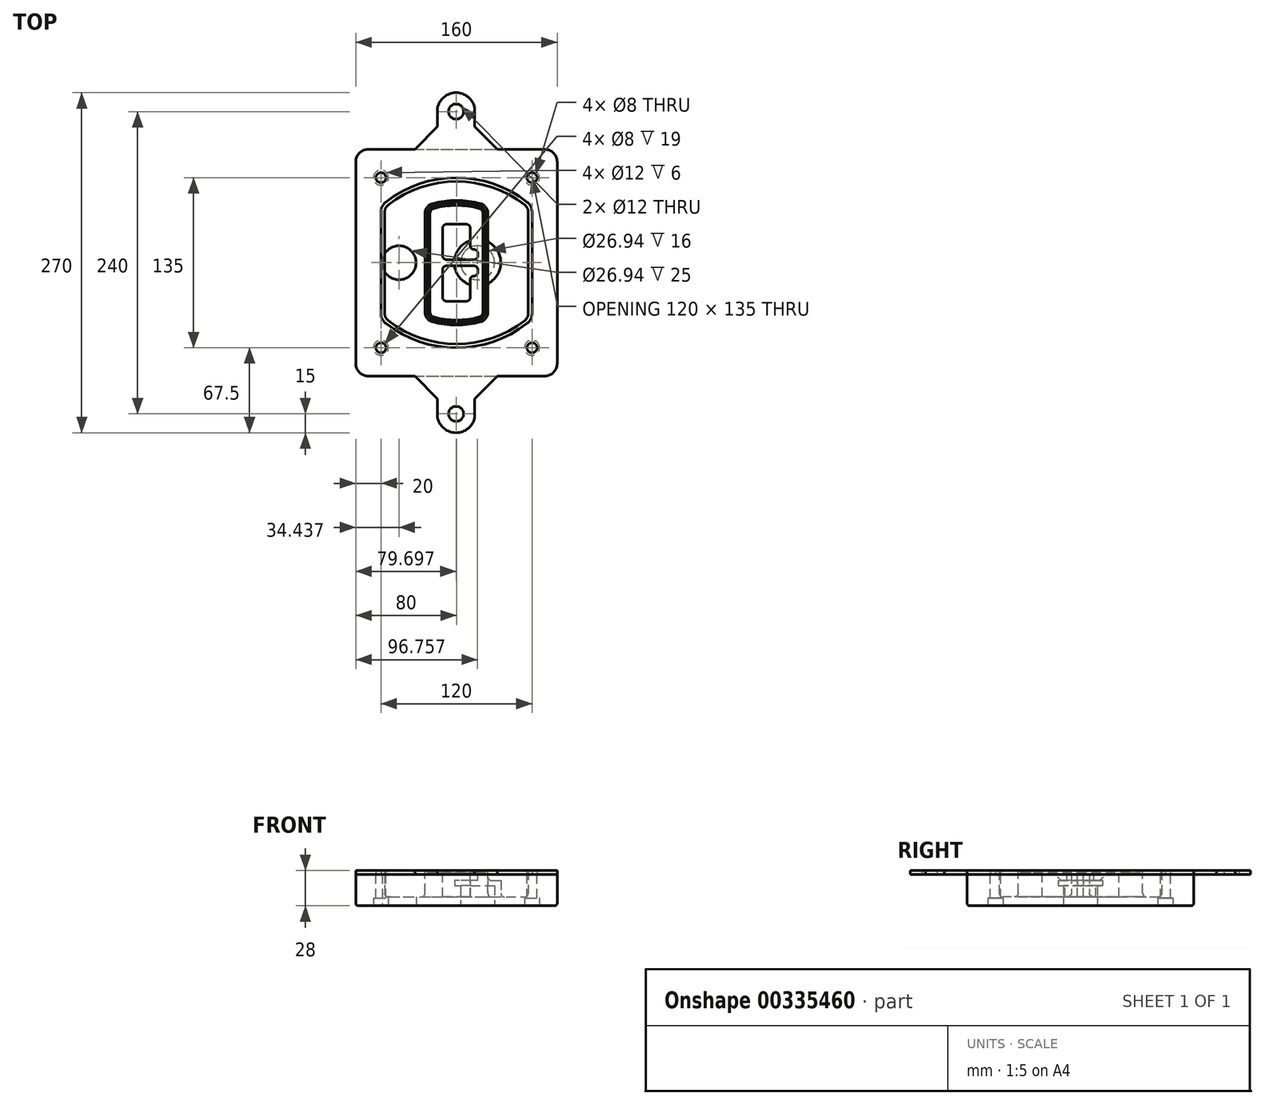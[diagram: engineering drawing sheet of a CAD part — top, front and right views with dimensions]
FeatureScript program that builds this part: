
annotation { "Feature Type Name" : "Feature", "Feature Type Description" : "" }
export const myFeature = defineFeature(function(context is Context, id is Id, definition is map)
    precondition{}
    {
        {
            var Q0;
            Q0=qCreatedBy(makeId("Top.planeOp"),FACE);
            var sketch = newSketch(context, id + "F0", { "sketchPlane" : qUnion([Q0])});
            skPoint(sketch, "E0.rect.middle", {"position": v(0, 0) * mm});
            skLineSegment(sketch, "E1.bottom", {"start": v(-70, -90) * mm, "end": v(70, -90) * mm});
            skLineSegment(sketch, "E1.top", {"start": v(-70, 90) * mm, "end": v(70, 90) * mm});
            skLineSegment(sketch, "E1.left", {"start": v(-80, -80) * mm, "end": v(-80, 80) * mm});
            skLineSegment(sketch, "E1.right", {"start": v(80, -80) * mm, "end": v(80, 80) * mm});
            skLineSegment(sketch, "E2", {"start": v(-80, 90) * mm, "end": v(80, -90) * mm, "construction": true});
            skLineSegment(sketch, "E3", {"start": v(80, 90) * mm, "end": v(-80, -90) * mm, "construction": true});
            skCircle(sketch, "E4", {"center": v(-60, 67.5) * mm, "radius": 4 * mm});
            skCircle(sketch, "E5", {"center": v(60, 67.5) * mm, "radius": 4 * mm});
            skCircle(sketch, "E6", {"center": v(60, -67.5) * mm, "radius": 4 * mm});
            skCircle(sketch, "E7", {"center": v(-60, -67.5) * mm, "radius": 4 * mm});
            skLineSegment(sketch, "E8", {"start": v(-60, 67.5) * mm, "end": v(60, 67.5) * mm, "construction": true});
            skLineSegment(sketch, "E9", {"start": v(60, 67.5) * mm, "end": v(60, -67.5) * mm, "construction": true});
            skLineSegment(sketch, "E10", {"start": v(60, -67.5) * mm, "end": v(-60, -67.5) * mm, "construction": true});
            skLineSegment(sketch, "E11", {"start": v(-60, -67.5) * mm, "end": v(-60, 67.5) * mm, "construction": true});
            skLineSegment(sketch, "E12", {"start": v(-60, 40.3) * mm, "end": v(-60, -40.3) * mm});
            skLineSegment(sketch, "E13", {"start": v(60, 40.3) * mm, "end": v(60, -40.3) * mm});
            skArc(sketch, "E14", {"start": v(56.15, 48.18) * mm, "mid": v(0, 67.5) * mm, "end": v(-56.15, 48.18) * mm});
            skArc(sketch, "E15", {"start": v(-56.15, -48.18) * mm, "mid": v(0, -67.5) * mm, "end": v(56.15, -48.18) * mm});
            skLineSegment(sketch, "E16", {"start": v(-60, 0) * mm, "end": v(60, 0) * mm, "construction": true});
            skPoint(sketch, "E17.visualSharp", {"position": v(-60, -45) * mm});
            skArc(sketch, "E17.filletArc", {"start": v(-60, -40.3) * mm, "mid": v(-58.99, -44.68) * mm, "end": v(-56.15, -48.18) * mm});
            skPoint(sketch, "E18.visualSharp", {"position": v(-60, 45) * mm});
            skArc(sketch, "E18.filletArc", {"start": v(-56.15, 48.18) * mm, "mid": v(-58.99, 44.68) * mm, "end": v(-60, 40.3) * mm});
            skPoint(sketch, "E19.visualSharp", {"position": v(60, 45) * mm});
            skArc(sketch, "E19.filletArc", {"start": v(60, 40.3) * mm, "mid": v(58.99, 44.68) * mm, "end": v(56.15, 48.18) * mm});
            skPoint(sketch, "E20.visualSharp", {"position": v(60, -45) * mm});
            skArc(sketch, "E20.filletArc", {"start": v(56.15, -48.18) * mm, "mid": v(58.99, -44.68) * mm, "end": v(60, -40.3) * mm});
            skPoint(sketch, "E21.visualSharp", {"position": v(-80, 90) * mm});
            skArc(sketch, "E21.filletArc", {"start": v(-70, 90) * mm, "mid": v(-77.07, 87.07) * mm, "end": v(-80, 80) * mm});
            skPoint(sketch, "E22.visualSharp", {"position": v(80, 90) * mm});
            skArc(sketch, "E22.filletArc", {"start": v(80, 80) * mm, "mid": v(77.07, 87.07) * mm, "end": v(70, 90) * mm});
            skPoint(sketch, "E23.visualSharp", {"position": v(80, -90) * mm});
            skArc(sketch, "E23.filletArc", {"start": v(70, -90) * mm, "mid": v(77.07, -87.07) * mm, "end": v(80, -80) * mm});
            skPoint(sketch, "E24.visualSharp", {"position": v(-80, -90) * mm});
            skArc(sketch, "E24.filletArc", {"start": v(-80, -80) * mm, "mid": v(-77.07, -87.07) * mm, "end": v(-70, -90) * mm});
            skArc(sketch, "E25.0", {"start": v(57, 40.3) * mm, "mid": v(56.3, 43.36) * mm, "end": v(54.3, 45.81) * mm});
            skLineSegment(sketch, "E25.1", {"start": v(57, 40.3) * mm, "end": v(57, -40.3) * mm});
            skArc(sketch, "E25.2", {"start": v(54.3, -45.81) * mm, "mid": v(56.3, -43.36) * mm, "end": v(57, -40.3) * mm});
            skArc(sketch, "E25.3", {"start": v(-54.3, -45.81) * mm, "mid": v(0, -64.5) * mm, "end": v(54.3, -45.81) * mm});
            skArc(sketch, "E25.4", {"start": v(-57, -40.3) * mm, "mid": v(-56.3, -43.36) * mm, "end": v(-54.3, -45.81) * mm});
            skArc(sketch, "E25.5", {"start": v(54.3, 45.81) * mm, "mid": v(0, 64.5) * mm, "end": v(-54.3, 45.81) * mm});
            skLineSegment(sketch, "E25.6", {"start": v(-57, 40.3) * mm, "end": v(-57, -40.3) * mm});
            skArc(sketch, "E25.7", {"start": v(-54.3, 45.81) * mm, "mid": v(-56.3, 43.36) * mm, "end": v(-57, 40.3) * mm});
            skArc(sketch, "E26.0", {"start": v(-58.62, 51.33) * mm, "mid": v(-62.58, 46.43) * mm, "end": v(-64, 40.3) * mm});
            skArc(sketch, "E26.1", {"start": v(58.62, 51.33) * mm, "mid": v(0, 71.5) * mm, "end": v(-58.62, 51.33) * mm});
            skArc(sketch, "E26.2", {"start": v(64, 40.3) * mm, "mid": v(62.58, 46.43) * mm, "end": v(58.62, 51.33) * mm});
            skLineSegment(sketch, "E26.3", {"start": v(64, 40.3) * mm, "end": v(64, -40.3) * mm});
            skArc(sketch, "E26.4", {"start": v(58.62, -51.33) * mm, "mid": v(62.58, -46.43) * mm, "end": v(64, -40.3) * mm});
            skLineSegment(sketch, "E26.5", {"start": v(-64, 40.3) * mm, "end": v(-64, -40.3) * mm});
            skArc(sketch, "E26.6", {"start": v(-58.62, -51.33) * mm, "mid": v(0, -71.5) * mm, "end": v(58.62, -51.33) * mm});
            skArc(sketch, "E26.7", {"start": v(-64, -40.3) * mm, "mid": v(-62.58, -46.43) * mm, "end": v(-58.62, -51.33) * mm});
            skSolve(sketch);
        }
        {
            var Q0;
            Q0=makeQuery(id+"F0.imprint","IMPRINT",FACE,{"disambiguationData":[TD([[makeQuery(id+"F0.imprint","IMPRINT",EDGE,{"derivedFrom":sQuery(id+"F0.wireOp",EDGE,"E1.bottom")}),1.0]])]});
            var Q1;
            Q1=makeQuery(id+"F0.imprint","IMPRINT",FACE,{"disambiguationData":[TD([[makeQuery(id+"F0.imprint","IMPRINT",EDGE,{"derivedFrom":sQuery(id+"F0.wireOp",EDGE,"E12")}),1.0]])]});
            var Q2;
            Q2=makeQuery(id+"F0.imprint","IMPRINT",FACE,{"disambiguationData":[TD([[makeQuery(id+"F0.imprint","IMPRINT",EDGE,{"derivedFrom":sQuery(id+"F0.wireOp",EDGE,"E25.0")}),1.0]])]});
            var Q3;
            Q3=makeQuery(id+"F0.imprint","IMPRINT",FACE,{"disambiguationData":[TD([[makeQuery(id+"F0.imprint","IMPRINT",EDGE,{"derivedFrom":sQuery(id+"F0.wireOp",EDGE,"E12")}),-1.0]])]});
            extrude(context, id + "F1", {"entities" : qUnion([Q0, Q1, Q2, Q3]), "oppositeDirection" : true, "depth" : 25 * mm});
        }
        {
            var Q0;
            Q0=makeQuery(id+"F0.imprint","IMPRINT",FACE,{"disambiguationData":[TD([[makeQuery(id+"F0.imprint","IMPRINT",EDGE,{"derivedFrom":sQuery(id+"F0.wireOp",EDGE,"E12")}),1.0]])]});
            extrude(context, id + "F2", {"entities" : qUnion([Q0]), "operationType" : NewBodyOperationType.ADD, "depth" : 3 * mm});
        }
        {
            var Q0;
            Q0=makeQuery(id+"F0.imprint","IMPRINT",FACE,{"disambiguationData":[TD([[makeQuery(id+"F0.imprint","IMPRINT",EDGE,{"derivedFrom":sQuery(id+"F0.wireOp",EDGE,"E25.0")}),1.0]])]});
            extrude(context, id + "F3", {"entities" : qUnion([Q0]), "operationType" : NewBodyOperationType.REMOVE, "oppositeDirection" : true, "depth" : 18 * mm});
        }
        {
            var Q0;
            Q0=makeQuery(id+"F2.opExtrude","CAP_FACE",FACE,{"disambiguationData":[OSD([sQuery(id+"F0.wireOp",EDGE,"E12"),sQuery(id+"F0.wireOp",EDGE,"E13"),sQuery(id+"F0.wireOp",EDGE,"E14"),sQuery(id+"F0.wireOp",EDGE,"E15"),sQuery(id+"F0.wireOp",EDGE,"E17.filletArc"),sQuery(id+"F0.wireOp",EDGE,"E18.filletArc"),sQuery(id+"F0.wireOp",EDGE,"E19.filletArc"),sQuery(id+"F0.wireOp",EDGE,"E20.filletArc"),sQuery(id+"F0.wireOp",EDGE,"E25.0"),sQuery(id+"F0.wireOp",EDGE,"E25.1"),sQuery(id+"F0.wireOp",EDGE,"E25.2"),sQuery(id+"F0.wireOp",EDGE,"E25.3"),sQuery(id+"F0.wireOp",EDGE,"E25.4"),sQuery(id+"F0.wireOp",EDGE,"E25.5"),sQuery(id+"F0.wireOp",EDGE,"E25.6"),sQuery(id+"F0.wireOp",EDGE,"E25.7")])],"isStart":false});
            var sketch = newSketch(context, id + "F4", { "sketchPlane" : qUnion([Q0])});
            skArc(sketch, "E27.0", {"start": v(-19.08, -46.97) * mm, "mid": v(0, -49.5) * mm, "end": v(19.08, -46.97) * mm});
            skArc(sketch, "E28.0", {"start": v(19.08, 46.97) * mm, "mid": v(0, 49.5) * mm, "end": v(-19.08, 46.97) * mm});
            skLineSegment(sketch, "E29", {"start": v(-25, 39.25) * mm, "end": v(-25, -39.25) * mm});
            skLineSegment(sketch, "E30", {"start": v(25, 39.25) * mm, "end": v(25, -39.25) * mm});
            skLineSegment(sketch, "E31", {"start": v(-25, 45.1) * mm, "end": v(25, 45.1) * mm, "construction": true});
            skLineSegment(sketch, "E32", {"start": v(-25, -45.1) * mm, "end": v(25, -45.1) * mm, "construction": true});
            skPoint(sketch, "E33.visualSharp", {"position": v(-25, 45.1) * mm});
            skArc(sketch, "E33.filletArc", {"start": v(-19.08, 46.97) * mm, "mid": v(-23.35, 44.11) * mm, "end": v(-25, 39.25) * mm});
            skPoint(sketch, "E34.visualSharp", {"position": v(25, 45.1) * mm});
            skArc(sketch, "E34.filletArc", {"start": v(25, 39.25) * mm, "mid": v(23.35, 44.11) * mm, "end": v(19.08, 46.97) * mm});
            skPoint(sketch, "E35.visualSharp", {"position": v(25, -45.1) * mm});
            skArc(sketch, "E35.filletArc", {"start": v(19.08, -46.97) * mm, "mid": v(23.35, -44.11) * mm, "end": v(25, -39.25) * mm});
            skPoint(sketch, "E36.visualSharp", {"position": v(-25, -45.1) * mm});
            skArc(sketch, "E36.filletArc", {"start": v(-25, -39.25) * mm, "mid": v(-23.35, -44.11) * mm, "end": v(-19.08, -46.97) * mm});
            skArc(sketch, "E37.0", {"start": v(54.3, 45.81) * mm, "mid": v(0, 64.5) * mm, "end": v(-54.3, 45.81) * mm});
            skArc(sketch, "E37.1", {"start": v(-54.3, 45.81) * mm, "mid": v(-56.3, 43.36) * mm, "end": v(-57, 40.3) * mm});
            skLineSegment(sketch, "E37.2", {"start": v(-57, 40.3) * mm, "end": v(-57, -40.3) * mm});
            skArc(sketch, "E37.3", {"start": v(-57, -40.3) * mm, "mid": v(-56.3, -43.36) * mm, "end": v(-54.3, -45.81) * mm});
            skArc(sketch, "E37.4", {"start": v(-54.3, -45.81) * mm, "mid": v(0, -64.5) * mm, "end": v(54.3, -45.81) * mm});
            skArc(sketch, "E37.5", {"start": v(54.3, -45.81) * mm, "mid": v(56.3, -43.36) * mm, "end": v(57, -40.3) * mm});
            skLineSegment(sketch, "E37.6", {"start": v(57, 40.3) * mm, "end": v(57, -40.3) * mm});
            skArc(sketch, "E37.7", {"start": v(57, 40.3) * mm, "mid": v(56.3, 43.36) * mm, "end": v(54.3, 45.81) * mm});
            skLineSegment(sketch, "E38.0", {"start": v(23, 39.25) * mm, "end": v(23, -39.25) * mm});
            skArc(sketch, "E38.1", {"start": v(18.56, -45.04) * mm, "mid": v(21.76, -42.9) * mm, "end": v(23, -39.25) * mm});
            skArc(sketch, "E38.2", {"start": v(-18.56, -45.04) * mm, "mid": v(0, -47.5) * mm, "end": v(18.56, -45.04) * mm});
            skArc(sketch, "E38.3", {"start": v(-23, -39.25) * mm, "mid": v(-21.76, -42.9) * mm, "end": v(-18.56, -45.04) * mm});
            skLineSegment(sketch, "E38.4", {"start": v(-23, 39.25) * mm, "end": v(-23, -39.25) * mm});
            skArc(sketch, "E38.5", {"start": v(23, 39.25) * mm, "mid": v(21.76, 42.9) * mm, "end": v(18.56, 45.04) * mm});
            skArc(sketch, "E38.6", {"start": v(-18.56, 45.04) * mm, "mid": v(-21.76, 42.9) * mm, "end": v(-23, 39.25) * mm});
            skArc(sketch, "E38.7", {"start": v(18.56, 45.04) * mm, "mid": v(0, 47.5) * mm, "end": v(-18.56, 45.04) * mm});
            skArc(sketch, "E39.0", {"start": v(21, 39.25) * mm, "mid": v(20.18, 41.68) * mm, "end": v(18.04, 43.1) * mm});
            skLineSegment(sketch, "E39.1", {"start": v(21, 39.25) * mm, "end": v(21, -39.25) * mm});
            skArc(sketch, "E39.2", {"start": v(18.04, -43.1) * mm, "mid": v(20.18, -41.68) * mm, "end": v(21, -39.25) * mm});
            skArc(sketch, "E39.3", {"start": v(-18.04, -43.1) * mm, "mid": v(0, -45.5) * mm, "end": v(18.04, -43.1) * mm});
            skArc(sketch, "E39.4", {"start": v(-21, -39.25) * mm, "mid": v(-20.18, -41.68) * mm, "end": v(-18.04, -43.1) * mm});
            skArc(sketch, "E39.5", {"start": v(18.04, 43.1) * mm, "mid": v(0, 45.5) * mm, "end": v(-18.04, 43.1) * mm});
            skLineSegment(sketch, "E39.6", {"start": v(-21, 39.25) * mm, "end": v(-21, -39.25) * mm});
            skArc(sketch, "E39.7", {"start": v(-18.04, 43.1) * mm, "mid": v(-20.18, 41.68) * mm, "end": v(-21, 39.25) * mm});
            skLineSegment(sketch, "E40", {"start": v(-25, 0) * mm, "end": v(25, 0) * mm, "construction": true});
            skLineSegment(sketch, "E41", {"start": v(-11, 5.5) * mm, "end": v(-11, 27.5) * mm});
            skLineSegment(sketch, "E42", {"start": v(-8, 30.5) * mm, "end": v(8, 30.5) * mm});
            skLineSegment(sketch, "E43", {"start": v(11, 27.5) * mm, "end": v(11, 13.5) * mm});
            skLineSegment(sketch, "E44", {"start": v(14, 10.5) * mm, "end": v(14, 10.5) * mm});
            skLineSegment(sketch, "E45", {"start": v(17, 7.5) * mm, "end": v(17, 5.5) * mm});
            skLineSegment(sketch, "E46", {"start": v(14, 2.5) * mm, "end": v(-8, 2.5) * mm});
            skPoint(sketch, "E47.visualSharp", {"position": v(-11, 30.5) * mm});
            skArc(sketch, "E47.filletArc", {"start": v(-8, 30.5) * mm, "mid": v(-10.12, 29.62) * mm, "end": v(-11, 27.5) * mm});
            skPoint(sketch, "E48.visualSharp", {"position": v(11, 30.5) * mm});
            skArc(sketch, "E48.filletArc", {"start": v(11, 27.5) * mm, "mid": v(10.12, 29.62) * mm, "end": v(8, 30.5) * mm});
            skPoint(sketch, "E49.visualSharp", {"position": v(11, 10.5) * mm});
            skArc(sketch, "E49.filletArc", {"start": v(11, 13.5) * mm, "mid": v(11.88, 11.38) * mm, "end": v(14, 10.5) * mm});
            skPoint(sketch, "E50.visualSharp", {"position": v(17, 10.5) * mm});
            skArc(sketch, "E50.filletArc", {"start": v(17, 7.5) * mm, "mid": v(16.12, 9.62) * mm, "end": v(14, 10.5) * mm});
            skPoint(sketch, "E51.visualSharp", {"position": v(17, 2.5) * mm});
            skArc(sketch, "E51.filletArc", {"start": v(14, 2.5) * mm, "mid": v(16.12, 3.38) * mm, "end": v(17, 5.5) * mm});
            skPoint(sketch, "E52.visualSharp", {"position": v(-11, 2.5) * mm});
            skArc(sketch, "E52.filletArc", {"start": v(-11, 5.5) * mm, "mid": v(-10.12, 3.38) * mm, "end": v(-8, 2.5) * mm});
            skLineSegment(sketch, "E53.0.MirrorCS", {"start": v(14, -2.5) * mm, "end": v(-8, -2.5) * mm});
            skArc(sketch, "E54.0.MirrorCS", {"start": v(-11, -5.5) * mm, "mid": v(-10.12, -3.38) * mm, "end": v(-8, -2.5) * mm});
            skLineSegment(sketch, "E55.0.MirrorCS", {"start": v(-11, -5.5) * mm, "end": v(-11, -27.5) * mm});
            skArc(sketch, "E56.0.MirrorCS", {"start": v(-8, -30.5) * mm, "mid": v(-10.12, -29.62) * mm, "end": v(-11, -27.5) * mm});
            skLineSegment(sketch, "E57.0.MirrorCS", {"start": v(-8, -30.5) * mm, "end": v(8, -30.5) * mm});
            skArc(sketch, "E58.0.MirrorCS", {"start": v(11, -27.5) * mm, "mid": v(10.12, -29.62) * mm, "end": v(8, -30.5) * mm});
            skLineSegment(sketch, "E59.0.MirrorCS", {"start": v(11, -27.5) * mm, "end": v(11, -13.5) * mm});
            skArc(sketch, "E60.0.MirrorCS", {"start": v(11, -13.5) * mm, "mid": v(11.88, -11.38) * mm, "end": v(14, -10.5) * mm});
            skArc(sketch, "E61.0.MirrorCS", {"start": v(17, -7.5) * mm, "mid": v(16.12, -9.62) * mm, "end": v(14, -10.5) * mm});
            skLineSegment(sketch, "E62.0.MirrorCS", {"start": v(17, -7.5) * mm, "end": v(17, -5.5) * mm});
            skArc(sketch, "E63.0.MirrorCS", {"start": v(14, -2.5) * mm, "mid": v(16.12, -3.38) * mm, "end": v(17, -5.5) * mm});
            skSolve(sketch);
        }
        {
            var Q0;
            Q0=makeQuery(id+"F4.imprint","IMPRINT",FACE,{"disambiguationData":[TD([[makeQuery(id+"F4.imprint","IMPRINT",EDGE,{"derivedFrom":sQuery(id+"F4.wireOp",EDGE,"E27.0")}),1.0]])]});
            var Q1;
            Q1=makeQuery(id+"F4.imprint","IMPRINT",FACE,{"disambiguationData":[TD([[makeQuery(id+"F4.imprint","IMPRINT",EDGE,{"derivedFrom":sQuery(id+"F4.wireOp",EDGE,"E38.0")}),-1.0]])]});
            var Q2;
            Q2=makeQuery(id+"F4.imprint","IMPRINT",FACE,{"disambiguationData":[TD([[makeQuery(id+"F4.imprint","IMPRINT",EDGE,{"derivedFrom":sQuery(id+"F4.wireOp",EDGE,"E39.0")}),1.0]])]});
            extrude(context, id + "F5", {"entities" : qUnion([Q0, Q1, Q2]), "operationType" : NewBodyOperationType.ADD, "endBound" : BoundingType.UP_TO_NEXT, "oppositeDirection" : true, "depth" : 25 * mm});
        }
        {
            var Q0;
            Q0=makeQuery(id+"F4.imprint","IMPRINT",FACE,{"disambiguationData":[TD([[makeQuery(id+"F4.imprint","IMPRINT",EDGE,{"derivedFrom":sQuery(id+"F4.wireOp",EDGE,"E38.0")}),-1.0]])]});
            extrude(context, id + "F6", {"entities" : qUnion([Q0]), "operationType" : NewBodyOperationType.REMOVE, "oppositeDirection" : true, "depth" : 2 * mm});
        }
        {
            var Q0;
            Q0=makeQuery(id+"F1.opExtrude","CAP_FACE",FACE,{"disambiguationData":[OSD([sQuery(id+"F0.wireOp",EDGE,"E1.bottom"),sQuery(id+"F0.wireOp",EDGE,"E1.top"),sQuery(id+"F0.wireOp",EDGE,"E1.left"),sQuery(id+"F0.wireOp",EDGE,"E1.right"),sQuery(id+"F0.wireOp",EDGE,"E4"),sQuery(id+"F0.wireOp",EDGE,"E5"),sQuery(id+"F0.wireOp",EDGE,"E6"),sQuery(id+"F0.wireOp",EDGE,"E7"),sQuery(id+"F0.wireOp",EDGE,"E21.filletArc"),sQuery(id+"F0.wireOp",EDGE,"E22.filletArc"),sQuery(id+"F0.wireOp",EDGE,"E23.filletArc"),sQuery(id+"F0.wireOp",EDGE,"E24.filletArc")])],"isStart":false});
            var sketch = newSketch(context, id + "F7", { "sketchPlane" : qUnion([Q0])});
            skCircle(sketch, "E64", {"center": v(16.76, 0) * mm, "radius": 13.47 * mm});
            skCircle(sketch, "E65", {"center": v(-45.56, 0) * mm, "radius": 13.47 * mm});
            skLineSegment(sketch, "E66", {"start": v(80, 0) * mm, "end": v(-80, 0) * mm});
            skCircle(sketch, "E67", {"center": v(16.76, 0) * mm, "radius": 18.47 * mm});
            skCircle(sketch, "E68", {"center": v(60, -67.5) * mm, "radius": 6 * mm});
            skCircle(sketch, "E69", {"center": v(-60, -67.5) * mm, "radius": 6 * mm});
            skCircle(sketch, "E70", {"center": v(-60, 67.5) * mm, "radius": 6 * mm});
            skCircle(sketch, "E71", {"center": v(60, 67.5) * mm, "radius": 6 * mm});
            skSolve(sketch);
        }
        {
            var Q0;
            {var subQ1=sQuery(id+"F7.wireOp",EDGE,"E66");var subQ4=sQuery(id+"F7.wireOp",EDGE,"E64");var subQ6=makeQuery(id+"F7.imprint","INTERSECT",VERTEX,{"disambiguationData":[OD(0.0)],"derivedFrom":[subQ4,subQ1]});Q0=makeQuery(id+"F7.imprint","IMPRINT",FACE,{"disambiguationData":[TD([[makeQuery(id+"F7.imprint","IMPRINT",EDGE,{"disambiguationData":[TD([[subQ6,-1.0]])],"derivedFrom":subQ4}),-1.0]])]});}
            var Q1;
            {var subQ0=sQuery(id+"F7.wireOp",EDGE,"E66");var subQ1=sQuery(id+"F7.wireOp",EDGE,"E64");var subQ3=makeQuery(id+"F7.imprint","INTERSECT",VERTEX,{"disambiguationData":[OD(0.0)],"derivedFrom":[subQ1,subQ0]});Q1=makeQuery(id+"F7.imprint","IMPRINT",FACE,{"disambiguationData":[TD([[makeQuery(id+"F7.imprint","IMPRINT",EDGE,{"disambiguationData":[TD([[subQ3,-1.0]])],"derivedFrom":subQ1}),1.0]])]});}
            var Q2;
            {var subQ0=sQuery(id+"F7.wireOp",EDGE,"E66");var subQ1=sQuery(id+"F7.wireOp",EDGE,"E64");var subQ3=makeQuery(id+"F7.imprint","INTERSECT",VERTEX,{"disambiguationData":[OD(0.0)],"derivedFrom":[subQ1,subQ0]});Q2=makeQuery(id+"F7.imprint","IMPRINT",FACE,{"disambiguationData":[TD([[makeQuery(id+"F7.imprint","IMPRINT",EDGE,{"disambiguationData":[TD([[subQ3,1.0]])],"derivedFrom":subQ1}),1.0]])]});}
            var Q3;
            {var subQ1=sQuery(id+"F7.wireOp",EDGE,"E66");var subQ4=sQuery(id+"F7.wireOp",EDGE,"E64");var subQ6=makeQuery(id+"F7.imprint","INTERSECT",VERTEX,{"disambiguationData":[OD(0.0)],"derivedFrom":[subQ4,subQ1]});Q3=makeQuery(id+"F7.imprint","IMPRINT",FACE,{"disambiguationData":[TD([[makeQuery(id+"F7.imprint","IMPRINT",EDGE,{"disambiguationData":[TD([[subQ6,1.0]])],"derivedFrom":subQ4}),-1.0]])]});}
            extrude(context, id + "F8", {"entities" : qUnion([Q0, Q1, Q2, Q3]), "operationType" : NewBodyOperationType.ADD, "oppositeDirection" : true, "depth" : 20 * mm});
        }
        {
            var Q0;
            {var subQ0=sQuery(id+"F7.wireOp",EDGE,"E66");var subQ1=sQuery(id+"F7.wireOp",EDGE,"E64");var subQ3=makeQuery(id+"F7.imprint","INTERSECT",VERTEX,{"disambiguationData":[OD(0.0)],"derivedFrom":[subQ1,subQ0]});Q0=makeQuery(id+"F7.imprint","IMPRINT",FACE,{"disambiguationData":[TD([[makeQuery(id+"F7.imprint","IMPRINT",EDGE,{"disambiguationData":[TD([[subQ3,-1.0]])],"derivedFrom":subQ1}),1.0]])]});}
            var Q1;
            {var subQ0=sQuery(id+"F7.wireOp",EDGE,"E66");var subQ1=sQuery(id+"F7.wireOp",EDGE,"E64");var subQ3=makeQuery(id+"F7.imprint","INTERSECT",VERTEX,{"disambiguationData":[OD(0.0)],"derivedFrom":[subQ1,subQ0]});Q1=makeQuery(id+"F7.imprint","IMPRINT",FACE,{"disambiguationData":[TD([[makeQuery(id+"F7.imprint","IMPRINT",EDGE,{"disambiguationData":[TD([[subQ3,1.0]])],"derivedFrom":subQ1}),1.0]])]});}
            extrude(context, id + "F9", {"entities" : qUnion([Q0, Q1]), "operationType" : NewBodyOperationType.REMOVE, "oppositeDirection" : true, "depth" : 16 * mm});
        }
        {
            var Q0;
            {var subQ0=sQuery(id+"F7.wireOp",EDGE,"E66");var subQ1=sQuery(id+"F7.wireOp",EDGE,"E65");var subQ3=makeQuery(id+"F7.imprint","INTERSECT",VERTEX,{"disambiguationData":[OD(0.0)],"derivedFrom":[subQ1,subQ0]});Q0=makeQuery(id+"F7.imprint","IMPRINT",FACE,{"disambiguationData":[TD([[makeQuery(id+"F7.imprint","IMPRINT",EDGE,{"disambiguationData":[TD([[subQ3,-1.0]])],"derivedFrom":subQ1}),1.0]])]});}
            var Q1;
            {var subQ0=sQuery(id+"F7.wireOp",EDGE,"E66");var subQ1=sQuery(id+"F7.wireOp",EDGE,"E65");var subQ3=makeQuery(id+"F7.imprint","INTERSECT",VERTEX,{"disambiguationData":[OD(0.0)],"derivedFrom":[subQ1,subQ0]});Q1=makeQuery(id+"F7.imprint","IMPRINT",FACE,{"disambiguationData":[TD([[makeQuery(id+"F7.imprint","IMPRINT",EDGE,{"disambiguationData":[TD([[subQ3,1.0]])],"derivedFrom":subQ1}),1.0]])]});}
            extrude(context, id + "F10", {"entities" : qUnion([Q0, Q1]), "operationType" : NewBodyOperationType.REMOVE, "oppositeDirection" : true, "depth" : 25 * mm});
        }
        {
            var Q0;
            Q0=makeQuery(id+"F7.imprint","IMPRINT",FACE,{"disambiguationData":[TD([[makeQuery(id+"F7.imprint","IMPRINT",EDGE,{"derivedFrom":sQuery(id+"F7.wireOp",EDGE,"E68")}),1.0]])]});
            var Q1;
            Q1=makeQuery(id+"F7.imprint","IMPRINT",FACE,{"disambiguationData":[TD([[makeQuery(id+"F7.imprint","IMPRINT",EDGE,{"derivedFrom":makeQuery(id+"F1.opExtrude","CAP_EDGE",EDGE,{"disambiguationData":[OSD([sQuery(id+"F0.wireOp",EDGE,"E5")])],"isStart":false})}),-1.0]])]});
            var Q2;
            Q2=makeQuery(id+"F7.imprint","IMPRINT",FACE,{"disambiguationData":[TD([[makeQuery(id+"F7.imprint","IMPRINT",EDGE,{"derivedFrom":sQuery(id+"F7.wireOp",EDGE,"E69")}),1.0]])]});
            var Q3;
            Q3=makeQuery(id+"F7.imprint","IMPRINT",FACE,{"disambiguationData":[TD([[makeQuery(id+"F7.imprint","IMPRINT",EDGE,{"derivedFrom":makeQuery(id+"F1.opExtrude","CAP_EDGE",EDGE,{"disambiguationData":[OSD([sQuery(id+"F0.wireOp",EDGE,"E4")])],"isStart":false})}),-1.0]])]});
            var Q4;
            Q4=makeQuery(id+"F7.imprint","IMPRINT",FACE,{"disambiguationData":[TD([[makeQuery(id+"F7.imprint","IMPRINT",EDGE,{"derivedFrom":sQuery(id+"F7.wireOp",EDGE,"E70")}),1.0]])]});
            var Q5;
            Q5=makeQuery(id+"F7.imprint","IMPRINT",FACE,{"disambiguationData":[TD([[makeQuery(id+"F7.imprint","IMPRINT",EDGE,{"derivedFrom":makeQuery(id+"F1.opExtrude","CAP_EDGE",EDGE,{"disambiguationData":[OSD([sQuery(id+"F0.wireOp",EDGE,"E7")])],"isStart":false})}),-1.0]])]});
            var Q6;
            Q6=makeQuery(id+"F7.imprint","IMPRINT",FACE,{"disambiguationData":[TD([[makeQuery(id+"F7.imprint","IMPRINT",EDGE,{"derivedFrom":sQuery(id+"F7.wireOp",EDGE,"E71")}),1.0]])]});
            var Q7;
            Q7=makeQuery(id+"F7.imprint","IMPRINT",FACE,{"disambiguationData":[TD([[makeQuery(id+"F7.imprint","IMPRINT",EDGE,{"derivedFrom":makeQuery(id+"F1.opExtrude","CAP_EDGE",EDGE,{"disambiguationData":[OSD([sQuery(id+"F0.wireOp",EDGE,"E6")])],"isStart":false})}),-1.0]])]});
            extrude(context, id + "F11", {"entities" : qUnion([Q0, Q1, Q2, Q3, Q4, Q5, Q6, Q7]), "operationType" : NewBodyOperationType.REMOVE, "oppositeDirection" : true, "depth" : 6 * mm});
        }
        {
            var Q0;
            Q0=makeQuery(id+"F9.boolean.opBoolean","COPY",FACE,{"derivedFrom":makeQuery(id+"F9.opExtrude","CAP_FACE",FACE,{"disambiguationData":[OSD([sQuery(id+"F7.wireOp",EDGE,"E64")])],"isStart":false})});
            var sketch = newSketch(context, id + "F12", { "sketchPlane" : qUnion([Q0])});
            skArc(sketch, "E72.0", {"start": v(11, 17.55) * mm, "mid": v(2.57, 11.82) * mm, "end": v(-1.54, 2.5) * mm});
            skArc(sketch, "E72.1", {"start": v(-1.54, -2.5) * mm, "mid": v(2.57, -11.82) * mm, "end": v(11, -17.55) * mm});
            skLineSegment(sketch, "E73", {"start": v(-1.54, -2.5) * mm, "end": v(14, -2.5) * mm});
            skLineSegment(sketch, "E74.0", {"start": v(14, 2.5) * mm, "end": v(-1.54, 2.5) * mm});
            skArc(sketch, "E74.1", {"start": v(14, 2.5) * mm, "mid": v(16.12, 3.38) * mm, "end": v(17, 5.5) * mm});
            skLineSegment(sketch, "E74.2", {"start": v(17, 7.5) * mm, "end": v(17, 5.5) * mm});
            skArc(sketch, "E74.3", {"start": v(17, 7.5) * mm, "mid": v(16.12, 9.62) * mm, "end": v(14, 10.5) * mm});
            skArc(sketch, "E74.4", {"start": v(11, 13.5) * mm, "mid": v(11.88, 11.38) * mm, "end": v(14, 10.5) * mm});
            skLineSegment(sketch, "E74.5", {"start": v(11, 17.55) * mm, "end": v(11, 13.5) * mm});
            skLineSegment(sketch, "E74.7", {"start": v(14, -2.5) * mm, "end": v(-1.54, -2.5) * mm});
            skArc(sketch, "E74.8", {"start": v(14, -2.5) * mm, "mid": v(16.12, -3.38) * mm, "end": v(17, -5.5) * mm});
            skLineSegment(sketch, "E74.9", {"start": v(17, -7.5) * mm, "end": v(17, -5.5) * mm});
            skArc(sketch, "E74.10", {"start": v(17, -7.5) * mm, "mid": v(16.12, -9.62) * mm, "end": v(14, -10.5) * mm});
            skArc(sketch, "E74.11", {"start": v(11, -13.5) * mm, "mid": v(11.88, -11.38) * mm, "end": v(14, -10.5) * mm});
            skLineSegment(sketch, "E74.12", {"start": v(11, -17.55) * mm, "end": v(11, -13.5) * mm});
            skPoint(sketch, "E75.orphan", {"position": v(11, -27.5) * mm});
            skPoint(sketch, "E76.orphan", {"position": v(-8, -2.5) * mm});
            skPoint(sketch, "E77.orphan", {"position": v(-8, 2.5) * mm});
            skPoint(sketch, "E78.orphan", {"position": v(11, 27.5) * mm});
            skSolve(sketch);
        }
        {
            var Q0;
            {var subQ7=sQuery(id+"F12.wireOp",EDGE,"E72.0");var subQ14=sQuery(id+"F12.wireOp",EDGE,"E72.1");var subQ16=sQuery(id+"F12.wireOp",EDGE,"E74.1");var subQ18=sQuery(id+"F12.wireOp",EDGE,"E74.8");Q0=qUnion([makeQuery(id+"F12.imprint","IMPRINT",FACE,{"disambiguationData":[TD([[makeQuery(id+"F12.imprint","IMPRINT",EDGE,{"derivedFrom":subQ7}),1.0]])]}),makeQuery(id+"F12.imprint","IMPRINT",FACE,{"disambiguationData":[TD([[makeQuery(id+"F12.imprint","IMPRINT",EDGE,{"derivedFrom":subQ14}),1.0]])]}),makeQuery(id+"F12.imprint","IMPRINT",FACE,{"disambiguationData":[TD([[makeQuery(id+"F12.imprint","IMPRINT",EDGE,{"derivedFrom":subQ16}),1.0]])]}),makeQuery(id+"F12.imprint","IMPRINT",FACE,{"disambiguationData":[TD([[makeQuery(id+"F12.imprint","IMPRINT",EDGE,{"derivedFrom":subQ18}),-1.0]])]})]);}
            var Q1;
            Q1=makeQuery(id+"F5.boolean.opBoolean","SPLIT",FACE,{"disambiguationData":[TD([makeQuery(id+"F5.opExtrude","SWEPT_FACE",FACE,{"disambiguationData":[OSD([sQuery(id+"F4.wireOp",EDGE,"E41")])]})])],"derivedFrom":makeQuery(id+"F3.boolean.opBoolean","COPY",FACE,{"derivedFrom":makeQuery(id+"F3.opExtrude","CAP_FACE",FACE,{"disambiguationData":[OSD([sQuery(id+"F0.wireOp",EDGE,"E25.0"),sQuery(id+"F0.wireOp",EDGE,"E25.1"),sQuery(id+"F0.wireOp",EDGE,"E25.2"),sQuery(id+"F0.wireOp",EDGE,"E25.3"),sQuery(id+"F0.wireOp",EDGE,"E25.4"),sQuery(id+"F0.wireOp",EDGE,"E25.5"),sQuery(id+"F0.wireOp",EDGE,"E25.6"),sQuery(id+"F0.wireOp",EDGE,"E25.7")])],"isStart":false})})});
            extrude(context, id + "F13", {"entities" : qUnion([Q0]), "operationType" : NewBodyOperationType.REMOVE, "endBound" : BoundingType.UP_TO_SURFACE, "endBoundEntityFace" : qUnion([Q1]), "depth" : 25 * mm});
        }
        {
            var Q0;
            Q0=makeQuery(id+"F3.boolean.opBoolean","COPY",EDGE,{"derivedFrom":makeQuery(id+"F3.opExtrude","CAP_EDGE",EDGE,{"disambiguationData":[OSD([sQuery(id+"F0.wireOp",EDGE,"E25.6")])],"isStart":false})});
            var Q1;
            Q1=makeQuery(id+"F8.boolean.opBoolean","INTERSECT",EDGE,{"derivedFrom":[makeQuery(id+"F5.opExtrude","SWEPT_FACE",FACE,{"disambiguationData":[OSD([sQuery(id+"F4.wireOp",EDGE,"E30")])]}),makeQuery(id+"F8.opExtrude","CAP_FACE",FACE,{"disambiguationData":[OSD([sQuery(id+"F7.wireOp",EDGE,"E67")])],"isStart":false})]});
            var Q2;
            Q2=makeQuery(id+"F8.boolean.opBoolean","INTERSECT",EDGE,{"disambiguationData":[OD(1.0)],"derivedFrom":[makeQuery(id+"F5.opExtrude","SWEPT_FACE",FACE,{"disambiguationData":[OSD([sQuery(id+"F4.wireOp",EDGE,"E30")])]}),makeQuery(id+"F8.opExtrude","SWEPT_FACE",FACE,{"disambiguationData":[OSD([sQuery(id+"F7.wireOp",EDGE,"E67")])]})]});
            var Q3;
            {var subQ0=sQuery(id+"F4.wireOp",EDGE,"E30");Q3=makeQuery(id+"F8.boolean.opBoolean","SPLIT",EDGE,{"disambiguationData":[TD([makeQuery(id+"F5.opExtrude","SWEPT_FACE",FACE,{"disambiguationData":[OSD([sQuery(id+"F4.wireOp",EDGE,"E35.filletArc")])]})])],"derivedFrom":makeQuery(id+"F5.opExtrude","CAP_EDGE",EDGE,{"disambiguationData":[OSD([subQ0])],"isStart":false})});}
            var Q4;
            {var subQ0=sQuery(id+"F0.wireOp",EDGE,"E25.7");var subQ1=sQuery(id+"F0.wireOp",EDGE,"E25.1");var subQ2=sQuery(id+"F0.wireOp",EDGE,"E25.6");var subQ3=sQuery(id+"F0.wireOp",EDGE,"E25.5");var subQ4=sQuery(id+"F0.wireOp",EDGE,"E25.4");var subQ5=sQuery(id+"F0.wireOp",EDGE,"E25.0");var subQ6=sQuery(id+"F0.wireOp",EDGE,"E25.2");var subQ7=sQuery(id+"F0.wireOp",EDGE,"E25.3");Q4=makeQuery(id+"F8.boolean.opBoolean","INTERSECT",EDGE,{"derivedFrom":[makeQuery(id+"F5.boolean.opBoolean","SPLIT",FACE,{"disambiguationData":[TD([makeQuery(id+"F2.opExtrude","SWEPT_FACE",FACE,{"disambiguationData":[OSD([subQ5])]})])],"derivedFrom":makeQuery(id+"F3.boolean.opBoolean","COPY",FACE,{"derivedFrom":makeQuery(id+"F3.opExtrude","CAP_FACE",FACE,{"disambiguationData":[OSD([subQ5,subQ1,subQ6,subQ7,subQ4,subQ3,subQ2,subQ0])],"isStart":false})})}),makeQuery(id+"F8.opExtrude","SWEPT_FACE",FACE,{"disambiguationData":[OSD([sQuery(id+"F7.wireOp",EDGE,"E67")])]})]});}
            var Q5;
            Q5=makeQuery(id+"F8.boolean.opBoolean","INTERSECT",EDGE,{"disambiguationData":[OD(0.0)],"derivedFrom":[makeQuery(id+"F5.opExtrude","SWEPT_FACE",FACE,{"disambiguationData":[OSD([sQuery(id+"F4.wireOp",EDGE,"E30")])]}),makeQuery(id+"F8.opExtrude","SWEPT_FACE",FACE,{"disambiguationData":[OSD([sQuery(id+"F7.wireOp",EDGE,"E67")])]})]});
            fillet(context, id + "F14", {"entities" : qUnion([Q0, Q1, Q2, Q3, Q4, Q5]), "radius" : 3 * mm, "tangentPropagation" : true, "allowEdgeOverflow" : false});
        }
        {
            var Q0;
            Q0=makeQuery(id+"F1.opExtrude","CAP_EDGE",EDGE,{"disambiguationData":[OSD([sQuery(id+"F0.wireOp",EDGE,"E1.bottom")])],"isStart":false});
            fillet(context, id + "F15", {"entities" : qUnion([Q0]), "radius" : 2 * mm, "tangentPropagation" : true, "allowEdgeOverflow" : false});
        }
        {
            var Q0;
            Q0=qCreatedBy(makeId("Top.planeOp"),FACE);
            var sketch = newSketch(context, id + "F16", { "sketchPlane" : qUnion([Q0])});
            skLineSegment(sketch, "E79.0", {"start": v(-80, -80) * mm, "end": v(-80, 80) * mm});
            skLineSegment(sketch, "E79.1", {"start": v(-70, -90) * mm, "end": v(70, -90) * mm});
            skLineSegment(sketch, "E79.2", {"start": v(80, -80) * mm, "end": v(80, 80) * mm});
            skLineSegment(sketch, "E79.3", {"start": v(-70, 90) * mm, "end": v(70, 90) * mm});
            skCircle(sketch, "E79.4", {"center": v(60, 67.5) * mm, "radius": 4 * mm});
            skCircle(sketch, "E79.5", {"center": v(-60, 67.5) * mm, "radius": 4 * mm});
            skCircle(sketch, "E79.6", {"center": v(-60, -67.5) * mm, "radius": 4 * mm});
            skCircle(sketch, "E79.7", {"center": v(60, -67.5) * mm, "radius": 4 * mm});
            skArc(sketch, "E79.8", {"start": v(-56.15, -48.18) * mm, "mid": v(0, -67.5) * mm, "end": v(56.15, -48.18) * mm});
            skLineSegment(sketch, "E79.9", {"start": v(60, 40.3) * mm, "end": v(60, -40.3) * mm});
            skArc(sketch, "E79.10", {"start": v(56.15, 48.18) * mm, "mid": v(0, 67.5) * mm, "end": v(-56.15, 48.18) * mm});
            skLineSegment(sketch, "E79.11", {"start": v(-60, 40.3) * mm, "end": v(-60, -40.3) * mm});
            skArc(sketch, "E79.12", {"start": v(-56.15, 48.18) * mm, "mid": v(-58.99, 44.68) * mm, "end": v(-60, 40.3) * mm});
            skArc(sketch, "E79.13", {"start": v(-60, -40.3) * mm, "mid": v(-58.99, -44.68) * mm, "end": v(-56.15, -48.18) * mm});
            skArc(sketch, "E79.14", {"start": v(56.15, -48.18) * mm, "mid": v(58.99, -44.68) * mm, "end": v(60, -40.3) * mm});
            skArc(sketch, "E79.15", {"start": v(60, 40.3) * mm, "mid": v(58.99, 44.68) * mm, "end": v(56.15, 48.18) * mm});
            skArc(sketch, "E79.16", {"start": v(-70, 90) * mm, "mid": v(-77.07, 87.07) * mm, "end": v(-80, 80) * mm});
            skArc(sketch, "E79.17", {"start": v(80, 80) * mm, "mid": v(77.07, 87.07) * mm, "end": v(70, 90) * mm});
            skArc(sketch, "E79.18", {"start": v(70, -90) * mm, "mid": v(77.07, -87.07) * mm, "end": v(80, -80) * mm});
            skArc(sketch, "E79.19", {"start": v(-80, -80) * mm, "mid": v(-77.07, -87.07) * mm, "end": v(-70, -90) * mm});
            skPoint(sketch, "E80.endSnap0", {"position": v(0, 90) * mm});
            skCircle(sketch, "E81", {"center": v(-0.3, 120) * mm, "radius": 6 * mm});
            skLineSegment(sketch, "E82", {"start": v(32.4, 90) * mm, "end": v(14.4, 108) * mm});
            skLineSegment(sketch, "E83", {"start": v(14.4, 108) * mm, "end": v(14.4, 123) * mm});
            skArc(sketch, "E84", {"start": v(14.4, 123) * mm, "mid": v(-0.3, 135) * mm, "end": v(-15, 123) * mm});
            skLineSegment(sketch, "E85", {"start": v(-15, 123) * mm, "end": v(-15, 108) * mm});
            skLineSegment(sketch, "E86", {"start": v(-15, 108) * mm, "end": v(-33, 90) * mm});
            skLineSegment(sketch, "E87", {"start": v(0, 0) * mm, "end": v(-80, 0) * mm});
            skLineSegment(sketch, "E88", {"start": v(0, 0) * mm, "end": v(80, 0) * mm});
            skLineSegment(sketch, "E89.MirrorCS", {"start": v(-0.3, -96) * mm, "end": v(-0.3, -120) * mm});
            skArc(sketch, "E90.MirrorCS", {"start": v(14.4, -123) * mm, "mid": v(-0.3, -135) * mm, "end": v(-15, -123) * mm});
            skLineSegment(sketch, "E91.MirrorCS", {"start": v(32.4, -90) * mm, "end": v(14.4, -108) * mm});
            skLineSegment(sketch, "E92.MirrorCS", {"start": v(14.4, -108) * mm, "end": v(14.4, -123) * mm});
            skCircle(sketch, "E93.MirrorC", {"center": v(-0.3, -120) * mm, "radius": 6 * mm});
            skLineSegment(sketch, "E94.MirrorCS", {"start": v(-15, -123) * mm, "end": v(-15, -108) * mm});
            skLineSegment(sketch, "E95.MirrorCS", {"start": v(-15, -108) * mm, "end": v(-33, -90) * mm});
            skPoint(sketch, "E96.MirrorP", {"position": v(0, -108) * mm});
            skLineSegment(sketch, "E97", {"start": v(-0.3, 120) * mm, "end": v(0, 90) * mm});
            skSolve(sketch);
        }
        {
            var Q0;
            Q0 = qSketchRegion(id + "F16", true);
            var Q1;
            Q1=makeQuery(id+"F2.opExtrude","CAP_FACE",FACE,{"disambiguationData":[OSD([sQuery(id+"F0.wireOp",EDGE,"E12"),sQuery(id+"F0.wireOp",EDGE,"E13"),sQuery(id+"F0.wireOp",EDGE,"E14"),sQuery(id+"F0.wireOp",EDGE,"E15"),sQuery(id+"F0.wireOp",EDGE,"E17.filletArc"),sQuery(id+"F0.wireOp",EDGE,"E18.filletArc"),sQuery(id+"F0.wireOp",EDGE,"E19.filletArc"),sQuery(id+"F0.wireOp",EDGE,"E20.filletArc"),sQuery(id+"F0.wireOp",EDGE,"E25.0"),sQuery(id+"F0.wireOp",EDGE,"E25.1"),sQuery(id+"F0.wireOp",EDGE,"E25.2"),sQuery(id+"F0.wireOp",EDGE,"E25.3"),sQuery(id+"F0.wireOp",EDGE,"E25.4"),sQuery(id+"F0.wireOp",EDGE,"E25.5"),sQuery(id+"F0.wireOp",EDGE,"E25.6"),sQuery(id+"F0.wireOp",EDGE,"E25.7")])],"isStart":false});
            extrude(context, id + "F17", {"entities" : qUnion([Q0]), "endBound" : BoundingType.UP_TO_SURFACE, "endBoundEntityFace" : qUnion([Q1]), "depth" : 25 * mm});
        }
    });
